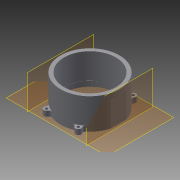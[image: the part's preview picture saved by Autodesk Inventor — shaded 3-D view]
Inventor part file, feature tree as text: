
AUTODESK INVENTOR PART (.ipt)
format: ipt  version: 2014 SP2 (Build 180246200, 246)  size: 211,968 bytes
history: native  units: mm
features: plane x5, extrude x4, sketch x4, reference x1, projected_geometry x1
ambient origin geometry x8: Origin, YZ Plane, XZ Plane, XY Plane, X Axis, Y Axis, Z Axis, Center Point
bodies: Solid1 (feature_tree)
feature tree (15):
  plane  "Work Plane1"
  extrude  "Extrusion1"  Depth=50.0mm TaperAngle=0.0deg
  extrude  "Extrusion2"  Depth=50.0mm TaperAngle=0.0deg
  plane  "Work Plane3"
  extrude  "Extrusion3"  [1 undecoded]
  plane  "Work Plane6"
  extrude  "Extrusion4"  [1 undecoded]
  sketch  "Sketch1"  dims[d0=10.0mm d1=0.0mm d2=50.0mm d3=0.0mm]
  reference  "Reference1"
  sketch  "Sketch2"  dims[d4=50.0mm d5=2.0mm d6=0.0mm]
  plane  "Work Plane2"
  sketch  "Sketch3"  dims[d7=2.0mm d8=0.0mm]
  plane  "Work Plane5"
  sketch  "Sketch4"
  projected_geometry  "Projected Loop1"
note: 2 required parameter values undecoded (feature->parameter linkage not recoverable at this tier; creation-order binding heuristic only, values carry confidence <= 0.55)
